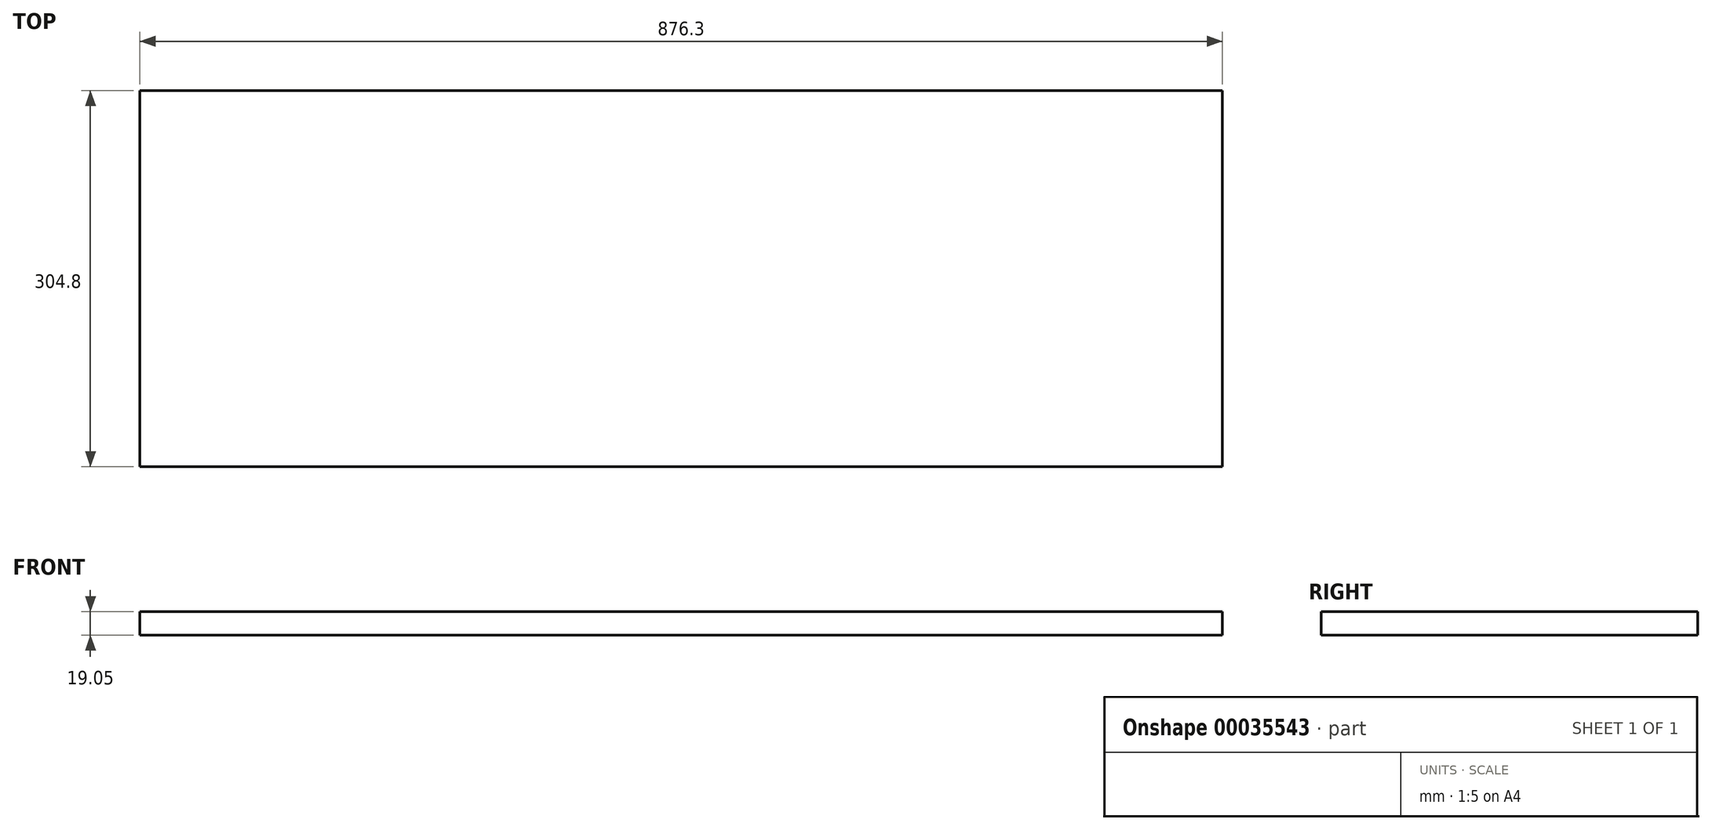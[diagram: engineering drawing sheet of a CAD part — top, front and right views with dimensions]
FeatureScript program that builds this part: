
annotation { "Feature Type Name" : "Feature", "Feature Type Description" : "" }
export const myFeature = defineFeature(function(context is Context, id is Id, definition is map)
    precondition{}
    {
        {
            var Q0;
            Q0=qCreatedBy(makeId("Top.planeOp"),FACE);
            var sketch = newSketch(context, id + "F0", { "sketchPlane" : qUnion([Q0])});
            skLineSegment(sketch, "E0.bottom", {"start": v(-436.44, 16.73) * mm, "end": v(439.86, 16.73) * mm});
            skLineSegment(sketch, "E0.top", {"start": v(-436.44, -288.07) * mm, "end": v(439.86, -288.07) * mm});
            skLineSegment(sketch, "E0.left", {"start": v(-436.44, 16.73) * mm, "end": v(-436.44, -288.07) * mm});
            skLineSegment(sketch, "E0.right", {"start": v(439.86, 16.73) * mm, "end": v(439.86, -288.07) * mm});
            skSolve(sketch);
        }
        {
            var Q0;
            Q0=qSketchRegion(id+"F0",true);
            extrude(context, id + "F1", {"entities" : qUnion([Q0]), "depth" : 19.05 * mm});
        }
    });
